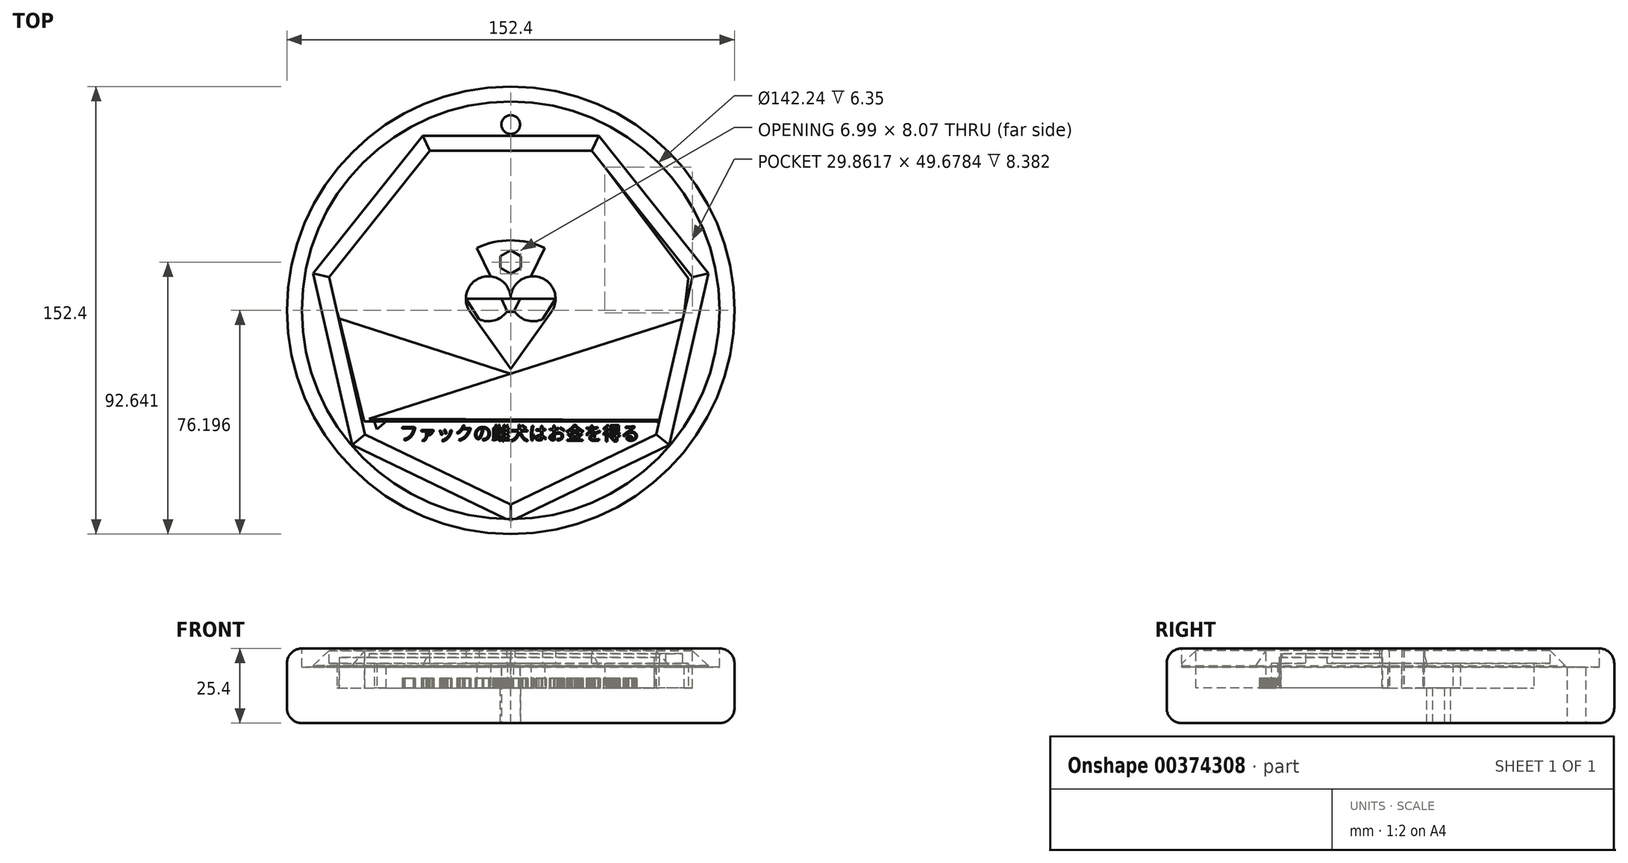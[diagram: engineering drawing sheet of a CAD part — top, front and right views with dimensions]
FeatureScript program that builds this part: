
annotation { "Feature Type Name" : "Feature", "Feature Type Description" : "" }
export const myFeature = defineFeature(function(context is Context, id is Id, definition is map)
    precondition{}
    {
        {
            var Q0;
            Q0=qCreatedBy(makeId("Top.planeOp"),FACE);
            var sketch = newSketch(context, id + "F0", { "sketchPlane" : qUnion([Q0])});
            skCircle(sketch, "E0", {"center": v(0, 2.77) * mm, "radius": 76.2 * mm});
            skSolve(sketch);
        }
        {
            var Q0;
            Q0 = qSketchRegion(id + "F0", true);
            extrude(context, id + "F1", {"entities" : qUnion([Q0]), "depth" : 25.4 * mm});
        }
        {
            var Q0;
            Q0=makeQuery(id+"F1.opExtrude","CAP_EDGE",EDGE,{"disambiguationData":[OSD([sQuery(id+"F0.wireOp",EDGE,"E0")])],"isStart":false});
            var Q1;
            Q1=makeQuery(id+"F1.opExtrude","SWEPT_FACE",FACE,{"disambiguationData":[OSD([sQuery(id+"F0.wireOp",EDGE,"E0")])]});
            fillet(context, id + "F2", {"entities" : qUnion([Q0, Q1]), "radius" : 5.08 * mm, "tangentPropagation" : true, "allowEdgeOverflow" : false});
        }
        {
            var Q0;
            Q0=qCreatedBy(makeId("Top.planeOp"),FACE);
            var sketch = newSketch(context, id + "F3", { "sketchPlane" : qUnion([Q0])});
            skLineSegment(sketch, "E1", {"start": v(0, 0) * mm, "end": v(0, 66.04) * mm});
            skSolve(sketch);
        }
        {
            var Q0;
            Q0=sQuery(id+"F3.wireOp",VERTEX,"E1.end");
            var Q1;
            Q1=makeQuery(id+"F1.opExtrude","SWEPT_BODY",BODY,{"disambiguationData":[OSD([sQuery(id+"F0.wireOp",EDGE,"E0")])]});
            hole(context, id + "F4", {"style" : HoleStyle.SIMPLE, "endStyle" : HoleEndStyle.THROUGH, "oppositeDirection" : true, "holeDiameter" : 6.35 * mm, "isTappedThrough" : true, "tappedDepth" : 12.7 * mm, "tapClearance" : 3, "locations" : qUnion([Q0]), "scope" : qUnion([Q1])});
        }
        {
            var Q0;
            Q0=makeQuery(id+"F1.opExtrude","CAP_FACE",FACE,{"disambiguationData":[OSD([sQuery(id+"F0.wireOp",EDGE,"E0")])],"isStart":false});
            extrude(context, id + "F5", {"entities" : qUnion([Q0]), "operationType" : NewBodyOperationType.REMOVE, "oppositeDirection" : true, "depth" : 6.35 * mm});
        }
        {
            var Q0;
            Q0=qCreatedBy(makeId("Top.planeOp"),FACE);
            var sketch = newSketch(context, id + "F6", { "sketchPlane" : qUnion([Q0])});
            skCircle(sketch, "E2.cCircle", {"center": v(0, 0) * mm, "radius": 62.23 * mm, "construction": true});
            skLineSegment(sketch, "E2.0", {"start": v(-29.97, 62.23) * mm, "end": v(29.97, 62.23) * mm});
            skLineSegment(sketch, "E2.1", {"start": v(29.97, 62.23) * mm, "end": v(67.34, 15.37) * mm});
            skLineSegment(sketch, "E2.2", {"start": v(67.34, 15.37) * mm, "end": v(54, -43.06) * mm});
            skLineSegment(sketch, "E2.3", {"start": v(54, -43.06) * mm, "end": v(0, -69.07) * mm});
            skLineSegment(sketch, "E2.4", {"start": v(0, -69.07) * mm, "end": v(-54, -43.06) * mm});
            skLineSegment(sketch, "E2.5", {"start": v(-54, -43.06) * mm, "end": v(-67.34, 15.37) * mm});
            skLineSegment(sketch, "E2.6", {"start": v(-67.34, 15.37) * mm, "end": v(-29.97, 62.23) * mm});
            skPoint(sketch, "E2.0.midPoint", {"position": v(0, 62.23) * mm});
            skSolve(sketch);
        }
        {
            var Q0;
            Q0 = qSketchRegion(id + "F6", true);
            extrude(context, id + "F7", {"entities" : qUnion([Q0]), "operationType" : NewBodyOperationType.ADD, "depth" : 24.64 * mm});
        }
        {
            var Q0;
            Q0=makeQuery(id+"F7.opExtrude","CAP_EDGE",EDGE,{"disambiguationData":[OSD([sQuery(id+"F6.wireOp",EDGE,"E2.6")])],"isStart":false});
            var Q1;
            Q1=makeQuery(id+"F7.opExtrude","CAP_EDGE",EDGE,{"disambiguationData":[OSD([sQuery(id+"F6.wireOp",EDGE,"E2.5")])],"isStart":false});
            var Q2;
            Q2=makeQuery(id+"F7.opExtrude","CAP_EDGE",EDGE,{"disambiguationData":[OSD([sQuery(id+"F6.wireOp",EDGE,"E2.4")])],"isStart":false});
            var Q3;
            Q3=makeQuery(id+"F7.opExtrude","CAP_EDGE",EDGE,{"disambiguationData":[OSD([sQuery(id+"F6.wireOp",EDGE,"E2.3")])],"isStart":false});
            var Q4;
            Q4=makeQuery(id+"F7.opExtrude","CAP_EDGE",EDGE,{"disambiguationData":[OSD([sQuery(id+"F6.wireOp",EDGE,"E2.2")])],"isStart":false});
            var Q5;
            Q5=makeQuery(id+"F7.opExtrude","CAP_EDGE",EDGE,{"disambiguationData":[OSD([sQuery(id+"F6.wireOp",EDGE,"E2.1")])],"isStart":false});
            var Q6;
            Q6=makeQuery(id+"F7.opExtrude","CAP_EDGE",EDGE,{"disambiguationData":[OSD([sQuery(id+"F6.wireOp",EDGE,"E2.0")])],"isStart":false});
            chamfer(context, id + "F8", {"entities" : qUnion([Q0, Q1, Q2, Q3, Q4, Q5, Q6]), "width" : 5.08 * mm, "tangentPropagation" : true});
        }
        {
            var Q0;
            Q0=makeQuery(id+"F7.opExtrude","CAP_FACE",FACE,{"disambiguationData":[OSD([sQuery(id+"F6.wireOp",EDGE,"E2.0"),sQuery(id+"F6.wireOp",EDGE,"E2.1"),sQuery(id+"F6.wireOp",EDGE,"E2.2"),sQuery(id+"F6.wireOp",EDGE,"E2.3"),sQuery(id+"F6.wireOp",EDGE,"E2.4"),sQuery(id+"F6.wireOp",EDGE,"E2.5"),sQuery(id+"F6.wireOp",EDGE,"E2.6")])],"isStart":false});
            extrude(context, id + "F9", {"entities" : qUnion([Q0]), "operationType" : NewBodyOperationType.REMOVE, "oppositeDirection" : true, "depth" : 12.7 * mm});
        }
        {
            var Q0;
            Q0=qCreatedBy(makeId("Top.planeOp"),FACE);
            var sketch = newSketch(context, id + "F10", { "sketchPlane" : qUnion([Q0])});
            skLineSegment(sketch, "E3", {"start": v(0, 34.9) * mm, "end": v(0, 6.7) * mm});
            skLineSegment(sketch, "E4", {"start": v(0, 6.7) * mm, "end": v(-15.24, 6.7) * mm});
            skLineSegment(sketch, "E5", {"start": v(0, 6.7) * mm, "end": v(15.24, 6.7) * mm});
            skCircle(sketch, "E6", {"center": v(-7.62, 6.7) * mm, "radius": 7.65 * mm});
            skCircle(sketch, "E7", {"center": v(7.62, 6.7) * mm, "radius": 7.65 * mm});
            skLineSegment(sketch, "E8", {"start": v(-15.24, 6.7) * mm, "end": v(0, -17.14) * mm});
            skLineSegment(sketch, "E9", {"start": v(15.24, 6.7) * mm, "end": v(0, -17.14) * mm});
            skLineSegment(sketch, "E10", {"start": v(-13.86, 2.28) * mm, "end": v(0, -17.14) * mm});
            skLineSegment(sketch, "E11", {"start": v(-13.86, 2.28) * mm, "end": v(13.87, 2.28) * mm});
            skLineSegment(sketch, "E12", {"start": v(13.87, 2.28) * mm, "end": v(0, -17.14) * mm});
            skSolve(sketch);
        }
        {
            var Q0;
            Q0 = qSketchRegion(id + "F10", true);
            extrude(context, id + "F11", {"entities" : qUnion([Q0]), "operationType" : NewBodyOperationType.ADD, "depth" : 25.4 * mm});
        }
        {
            var Q0;
            Q0=qCreatedBy(makeId("Top.planeOp"),FACE);
            var sketch = newSketch(context, id + "F12", { "sketchPlane" : qUnion([Q0])});
            skCircle(sketch, "E13", {"center": v(0, 0) * mm, "radius": 26.61 * mm});
            skLineSegment(sketch, "E14", {"start": v(-27.58, 57.4) * mm, "end": v(0, 0) * mm});
            skLineSegment(sketch, "E15", {"start": v(0, 0) * mm, "end": v(27.57, 57.4) * mm});
            skLineSegment(sketch, "E16", {"start": v(-45.54, -37.78) * mm, "end": v(0, 0) * mm});
            skLineSegment(sketch, "E17", {"start": v(54, -38.2) * mm, "end": v(0, 0) * mm});
            skLineSegment(sketch, "E18", {"start": v(-27.58, 57.4) * mm, "end": v(-63, 13.7) * mm});
            skLineSegment(sketch, "E19", {"start": v(-63, 13.7) * mm, "end": v(-45.54, -37.78) * mm});
            skLineSegment(sketch, "E20", {"start": v(27.57, 57.4) * mm, "end": v(60.53, 13.7) * mm});
            skLineSegment(sketch, "E21", {"start": v(60.53, 13.7) * mm, "end": v(54, -38.2) * mm});
            skLineSegment(sketch, "E22", {"start": v(-27.58, 57.4) * mm, "end": v(27.57, 57.4) * mm});
            skSolve(sketch);
        }
        {
            var Q0;
            Q0 = qSketchRegion(id + "F12", true);
            extrude(context, id + "F13", {"entities" : qUnion([Q0]), "operationType" : NewBodyOperationType.ADD, "depth" : 20.32 * mm});
        }
        {
            var Q0;
            Q0=qCreatedBy(makeId("Top.planeOp"),FACE);
            var sketch = newSketch(context, id + "F14", { "sketchPlane" : qUnion([Q0])});
            skLineSegment(sketch, "E23", {"start": v(50.53, -35.13) * mm, "end": v(-49.86, -35.13) * mm});
            skLineSegment(sketch, "E24", {"start": v(-49.86, -35.13) * mm, "end": v(-58.46, 0) * mm});
            skLineSegment(sketch, "E25", {"start": v(-58.46, 0) * mm, "end": v(50.53, -35.13) * mm});
            skSolve(sketch);
        }
        {
            var Q0;
            Q0 = qSketchRegion(id + "F14", true);
            extrude(context, id + "F15", {"entities" : qUnion([Q0]), "operationType" : NewBodyOperationType.ADD, "depth" : 22.35 * mm});
        }
        {
            var Q0;
            Q0=qCreatedBy(makeId("Top.planeOp"),FACE);
            var sketch = newSketch(context, id + "F16", { "sketchPlane" : qUnion([Q0])});
            skLineSegment(sketch, "E26", {"start": v(-49.63, -34.57) * mm, "end": v(59, 0) * mm});
            skLineSegment(sketch, "E27", {"start": v(59, 0) * mm, "end": v(50.6, -34.58) * mm});
            skLineSegment(sketch, "E28", {"start": v(50.6, -34.58) * mm, "end": v(-48.28, -34.14) * mm});
            skSolve(sketch);
        }
        {
            var Q0;
            Q0 = qSketchRegion(id + "F16", true);
            extrude(context, id + "F17", {"entities" : qUnion([Q0]), "operationType" : NewBodyOperationType.ADD, "depth" : 23.62 * mm});
        }
        {
            var Q0;
            Q0=qCreatedBy(makeId("Top.planeOp"),FACE);
            var sketch = newSketch(context, id + "F18", { "sketchPlane" : qUnion([Q0])});
            skText(sketch, "E29", { "text": "ファックの雌犬はお金を得る", "fontName": "NotoSansCJKjp-Regular.otf"});
            const initialGuessF18  = {"E29": [-0.03791, -0.04144, 1, 0, 0.00453]};
            skSetInitialGuess(sketch, initialGuessF18);
            skSolve(sketch);
        }
        {
            var Q0;
            Q0 = qSketchRegion(id + "F18", true);
            extrude(context, id + "F19", {"entities" : qUnion([Q0]), "operationType" : NewBodyOperationType.ADD, "depth" : 15.24 * mm});
        }
        {
            var Q0;
            {var subQ0=sQuery(id+"F12.wireOp",EDGE,"E14");var subQ11=sQuery(id+"F10.wireOp",EDGE,"E10");var subQ14=sQuery(id+"F6.wireOp",EDGE,"E2.6");var subQ15=sQuery(id+"F6.wireOp",EDGE,"E2.5");var subQ16=sQuery(id+"F6.wireOp",EDGE,"E2.4");var subQ17=sQuery(id+"F6.wireOp",EDGE,"E2.3");var subQ18=sQuery(id+"F6.wireOp",EDGE,"E2.2");var subQ19=sQuery(id+"F6.wireOp",EDGE,"E2.1");var subQ20=sQuery(id+"F6.wireOp",EDGE,"E2.0");Q0=makeQuery(id+"F13.boolean.opBoolean","SPLIT",FACE,{"disambiguationData":[TD([makeQuery(id+"F13.opExtrude","SWEPT_FACE",FACE,{"disambiguationData":[OSD([subQ0])]})])],"derivedFrom":makeQuery(id+"F11.boolean.opBoolean","SPLIT",FACE,{"disambiguationData":[TD([makeQuery(id+"F11.opExtrude","SWEPT_FACE",FACE,{"disambiguationData":[OSD([subQ11])]})])],"derivedFrom":makeQuery(id+"F9.boolean.opBoolean","COPY",FACE,{"derivedFrom":makeQuery(id+"F9.opExtrude","CAP_FACE",FACE,{"disambiguationData":[OSD([subQ20,subQ19,subQ18,subQ17,subQ16,subQ15,subQ14])],"isStart":false})})})});}
            var sketch = newSketch(context, id + "F20", { "sketchPlane" : qUnion([Q0])});
            skCircle(sketch, "E30.cCircle", {"center": v(0, 19.21) * mm, "radius": 3.5 * mm, "construction": true});
            skLineSegment(sketch, "E30.0", {"start": v(3.5, 21.23) * mm, "end": v(3.5, 17.2) * mm});
            skLineSegment(sketch, "E30.1", {"start": v(3.5, 17.2) * mm, "end": v(0, 15.18) * mm});
            skLineSegment(sketch, "E30.2", {"start": v(0, 15.18) * mm, "end": v(-3.5, 17.2) * mm});
            skLineSegment(sketch, "E30.3", {"start": v(-3.5, 17.2) * mm, "end": v(-3.5, 21.23) * mm});
            skLineSegment(sketch, "E30.4", {"start": v(-3.5, 21.23) * mm, "end": v(0, 23.24) * mm});
            skLineSegment(sketch, "E30.5", {"start": v(0, 23.24) * mm, "end": v(3.5, 21.23) * mm});
            skPoint(sketch, "E30.0.midPoint", {"position": v(3.5, 19.21) * mm});
            skSolve(sketch);
        }
        {
            var Q0;
            Q0 = qSketchRegion(id + "F20", true);
            extrude(context, id + "F21", {"entities" : qUnion([Q0]), "operationType" : NewBodyOperationType.REMOVE, "oppositeDirection" : true, "depth" : 25.4 * mm});
        }
    });
